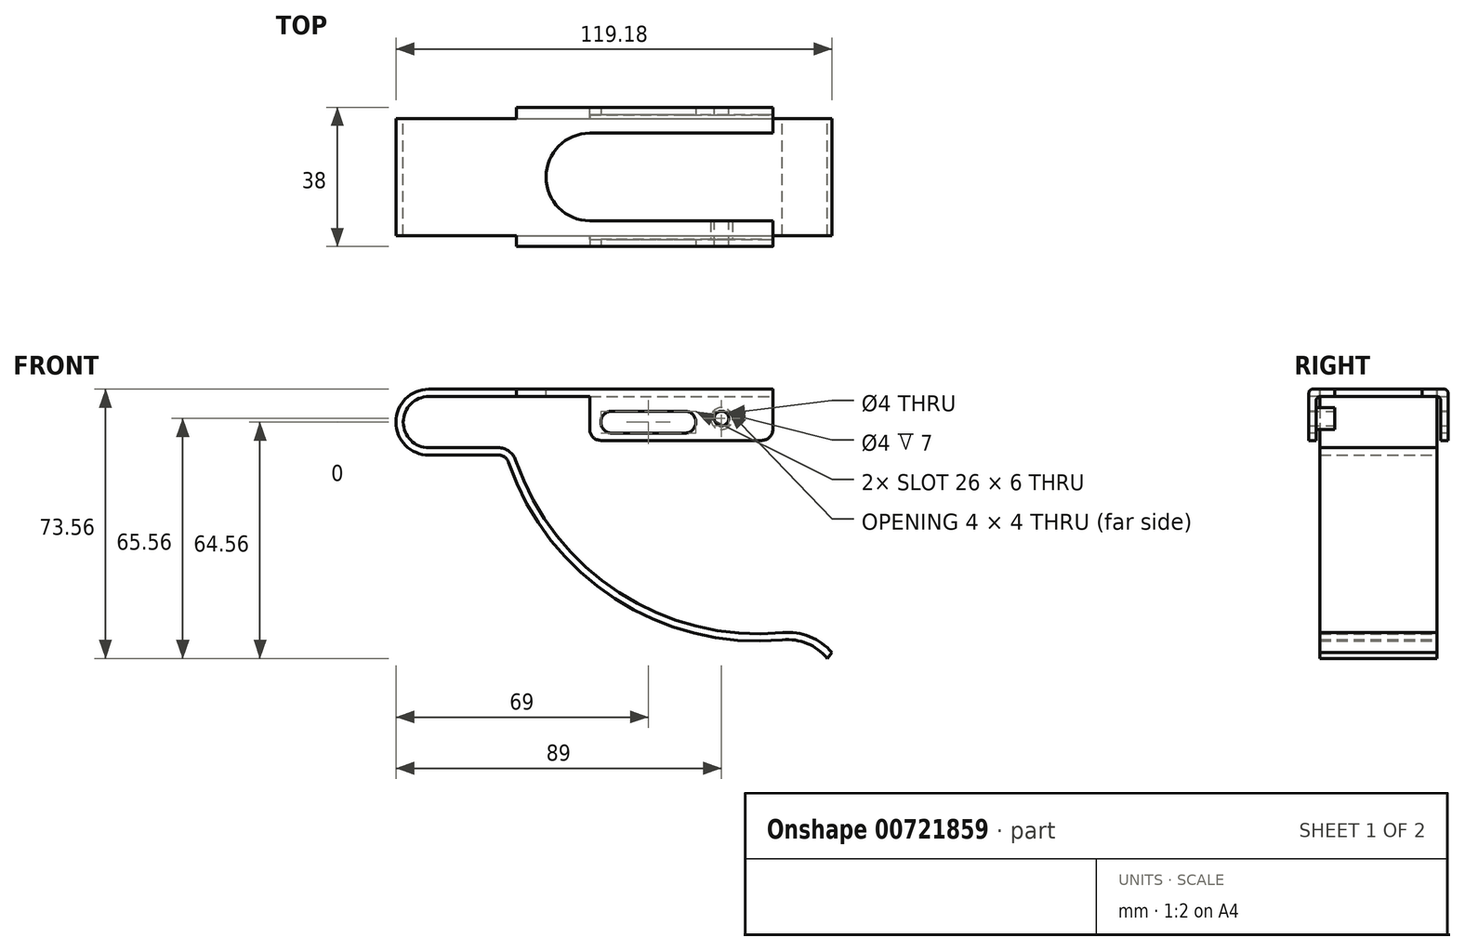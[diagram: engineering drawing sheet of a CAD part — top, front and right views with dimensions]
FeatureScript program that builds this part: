
annotation { "Feature Type Name" : "Feature", "Feature Type Description" : "" }
export const myFeature = defineFeature(function(context is Context, id is Id, definition is map)
    precondition{}
    {
        {
            var Q0;
            Q0=qCreatedBy(makeId("Front.planeOp"),FACE);
            var sketch = newSketch(context, id + "F0", { "sketchPlane" : qUnion([Q0])});
            skArc(sketch, "E0", {"start": v(0, 9) * mm, "mid": v(-9, 0) * mm, "end": v(0, -9) * mm});
            skLineSegment(sketch, "E1", {"start": v(0, 9) * mm, "end": v(94, 9) * mm});
            skLineSegment(sketch, "E2", {"start": v(0, -9) * mm, "end": v(19, -9) * mm});
            skArc(sketch, "E3", {"start": v(21.84, -11.03) * mm, "mid": v(50.83, -48.25) * mm, "end": v(96.64, -59.53) * mm});
            skArc(sketch, "E4", {"start": v(108.88, -64.56) * mm, "mid": v(103.39, -60.5) * mm, "end": v(96.64, -59.53) * mm});
            skPoint(sketch, "E5.visualSharp", {"position": v(21.18, -9) * mm});
            skArc(sketch, "E5.filletArc", {"start": v(21.84, -11.03) * mm, "mid": v(20.75, -9.56) * mm, "end": v(19, -9) * mm});
            skLineSegment(sketch, "E6.0", {"start": v(0, 7) * mm, "end": v(94, 7) * mm});
            skArc(sketch, "E6.1", {"start": v(0, 7) * mm, "mid": v(-7, 0) * mm, "end": v(0, -7) * mm});
            skArc(sketch, "E6.2", {"start": v(110.18, -63) * mm, "mid": v(104.1, -58.63) * mm, "end": v(96.7, -57.51) * mm});
            skArc(sketch, "E6.3", {"start": v(23.73, -10.39) * mm, "mid": v(52.02, -46.64) * mm, "end": v(96.7, -57.51) * mm});
            skArc(sketch, "E6.4", {"start": v(23.73, -10.39) * mm, "mid": v(21.91, -7.93) * mm, "end": v(19, -7) * mm});
            skLineSegment(sketch, "E6.5", {"start": v(0, -7) * mm, "end": v(19, -7) * mm});
            skLineSegment(sketch, "E7", {"start": v(94, 9) * mm, "end": v(94, 7) * mm});
            skLineSegment(sketch, "E8", {"start": v(110.18, -63) * mm, "end": v(108.88, -64.56) * mm});
            skSolve(sketch);
        }
        {
            var Q0;
            Q0 = qSketchRegion(id + "F0", true);
            extrude(context, id + "F1", {"entities" : qUnion([Q0]), "depth" : 16 * mm, "offsetDistance" : 25 * mm});
        }
        {
            var Q0;
            Q0=makeQuery(id+"F1.opExtrude","SWEPT_FACE",FACE,{"disambiguationData":[OSD([sQuery(id+"F0.wireOp",EDGE,"E1")])]});
            var sketch = newSketch(context, id + "F2", { "sketchPlane" : qUnion([Q0])});
            skLineSegment(sketch, "E9.bottom", {"start": v(94, -16) * mm, "end": v(24, -16) * mm});
            skLineSegment(sketch, "E9.top", {"start": v(94, -19) * mm, "end": v(24, -19) * mm});
            skLineSegment(sketch, "E9.left", {"start": v(94, -16) * mm, "end": v(94, -19) * mm});
            skLineSegment(sketch, "E9.right", {"start": v(24, -16) * mm, "end": v(24, -19) * mm});
            skSolve(sketch);
        }
        {
            var Q0;
            Q0 = qSketchRegion(id + "F2", true);
            extrude(context, id + "F3", {"entities" : qUnion([Q0]), "operationType" : NewBodyOperationType.ADD, "oppositeDirection" : true, "depth" : 2 * mm, "offsetDistance" : 25 * mm});
        }
        {
            var Q0;
            Q0=makeQuery(id+"F3.opExtrude","SWEPT_FACE",FACE,{"disambiguationData":[OSD([sQuery(id+"F2.wireOp",EDGE,"E9.top")])]});
            var sketch = newSketch(context, id + "F4", { "sketchPlane" : qUnion([Q0])});
            skLineSegment(sketch, "E10.bottom", {"start": v(94, 9) * mm, "end": v(44, 9) * mm});
            skLineSegment(sketch, "E10.top", {"start": v(94, -5) * mm, "end": v(44, -5) * mm});
            skLineSegment(sketch, "E10.left", {"start": v(94, 9) * mm, "end": v(94, -5) * mm});
            skLineSegment(sketch, "E10.right", {"start": v(44, 9) * mm, "end": v(44, -5) * mm});
            skSolve(sketch);
        }
        {
            var Q0;
            Q0 = qSketchRegion(id + "F4", true);
            extrude(context, id + "F5", {"entities" : qUnion([Q0]), "operationType" : NewBodyOperationType.ADD, "oppositeDirection" : true, "depth" : 2 * mm, "offsetDistance" : 25 * mm});
        }
        {
            var Q0;
            Q0=makeQuery(id+"F3.opExtrude","CAP_EDGE",EDGE,{"disambiguationData":[OSD([sQuery(id+"F2.wireOp",EDGE,"E9.top")])],"isStart":true});
            var Q1;
            Q1=makeQuery(id+"F5.boolean.opBoolean","INTERSECT",EDGE,{"derivedFrom":[makeQuery(id+"F3.boolean.opBoolean","MERGE",FACE,{"derivedFrom":[makeQuery(id+"F1.opExtrude","SWEPT_FACE",FACE,{"disambiguationData":[OSD([sQuery(id+"F0.wireOp",EDGE,"E6.0")])]}),makeQuery(id+"F3.opExtrude","CAP_FACE",FACE,{"disambiguationData":[OSD([sQuery(id+"F2.wireOp",EDGE,"E9.bottom"),sQuery(id+"F2.wireOp",EDGE,"E9.top"),sQuery(id+"F2.wireOp",EDGE,"E9.left"),sQuery(id+"F2.wireOp",EDGE,"E9.right")])],"isStart":false})]}),makeQuery(id+"F5.opExtrude","CAP_FACE",FACE,{"disambiguationData":[OSD([sQuery(id+"F4.wireOp",EDGE,"E10.bottom"),sQuery(id+"F4.wireOp",EDGE,"E10.top"),sQuery(id+"F4.wireOp",EDGE,"E10.left"),sQuery(id+"F4.wireOp",EDGE,"E10.right")])],"isStart":false})]});
            fillet(context, id + "F6", {"entities" : qUnion([Q0, Q1]), "radius" : 1 * mm, "allowEdgeOverflow" : false});
        }
        {
            var Q0;
            Q0=makeQuery(id+"F1.opExtrude","SWEPT_BODY",BODY,{"disambiguationData":[OSD([sQuery(id+"F0.wireOp",EDGE,"E0"),sQuery(id+"F0.wireOp",EDGE,"E1"),sQuery(id+"F0.wireOp",EDGE,"E2"),sQuery(id+"F0.wireOp",EDGE,"E3"),sQuery(id+"F0.wireOp",EDGE,"E4"),sQuery(id+"F0.wireOp",EDGE,"E5.filletArc"),sQuery(id+"F0.wireOp",EDGE,"E6.0"),sQuery(id+"F0.wireOp",EDGE,"E6.1"),sQuery(id+"F0.wireOp",EDGE,"E6.2"),sQuery(id+"F0.wireOp",EDGE,"E6.3"),sQuery(id+"F0.wireOp",EDGE,"E6.4"),sQuery(id+"F0.wireOp",EDGE,"E6.5"),sQuery(id+"F0.wireOp",EDGE,"E7"),sQuery(id+"F0.wireOp",EDGE,"E8")])]});
            var Q1;
            Q1=qCreatedBy(makeId("Front.planeOp"),FACE);
            mirror(context, id + "F7", {"operationType" : NewBodyOperationType.ADD, "entities" : qUnion([Q0]), "mirrorPlane" : qUnion([Q1])});
        }
        {
            var Q0;
            {var subQ0=makeQuery(id+"F3.boolean.opBoolean","MERGE",FACE,{"derivedFrom":[makeQuery(id+"F1.opExtrude","SWEPT_FACE",FACE,{"disambiguationData":[OSD([sQuery(id+"F0.wireOp",EDGE,"E1")])]}),makeQuery(id+"F3.opExtrude","CAP_FACE",FACE,{"disambiguationData":[OSD([sQuery(id+"F2.wireOp",EDGE,"E9.bottom"),sQuery(id+"F2.wireOp",EDGE,"E9.top"),sQuery(id+"F2.wireOp",EDGE,"E9.left"),sQuery(id+"F2.wireOp",EDGE,"E9.right")])],"isStart":true})]});Q0=makeQuery(id+"F7.boolean.opBoolean","MERGE",FACE,{"derivedFrom":[subQ0,makeQuery(id+"F7.opPattern","COPY",FACE,{"derivedFrom":subQ0,"instanceName":"1"})]});}
            var sketch = newSketch(context, id + "F8", { "sketchPlane" : qUnion([Q0])});
            skArc(sketch, "E11", {"start": v(44, 11.96) * mm, "mid": v(32.04, 0) * mm, "end": v(44, -11.96) * mm});
            skLineSegment(sketch, "E12", {"start": v(44, 11.96) * mm, "end": v(94, 11.96) * mm});
            skLineSegment(sketch, "E13", {"start": v(44, -11.96) * mm, "end": v(94, -11.96) * mm});
            skLineSegment(sketch, "E14", {"start": v(94, 11.96) * mm, "end": v(94, -11.96) * mm});
            skSolve(sketch);
        }
        {
            var Q0;
            Q0 = qSketchRegion(id + "F8", true);
            extrude(context, id + "F9", {"entities" : qUnion([Q0]), "operationType" : NewBodyOperationType.REMOVE, "oppositeDirection" : true, "depth" : 2 * mm, "offsetDistance" : 25 * mm});
        }
        {
            var Q0;
            Q0=makeQuery(id+"F5.boolean.opBoolean","MERGE",FACE,{"derivedFrom":[makeQuery(id+"F3.opExtrude","SWEPT_FACE",FACE,{"disambiguationData":[OSD([sQuery(id+"F2.wireOp",EDGE,"E9.top")])]}),makeQuery(id+"F5.opExtrude","CAP_FACE",FACE,{"disambiguationData":[OSD([sQuery(id+"F4.wireOp",EDGE,"E10.bottom"),sQuery(id+"F4.wireOp",EDGE,"E10.top"),sQuery(id+"F4.wireOp",EDGE,"E10.left"),sQuery(id+"F4.wireOp",EDGE,"E10.right")])],"isStart":true})]});
            var sketch = newSketch(context, id + "F10", { "sketchPlane" : qUnion([Q0])});
            skLineSegment(sketch, "E15", {"start": v(50, 0) * mm, "end": v(70, 0) * mm});
            skArc(sketch, "E16.0.startCap", {"start": v(50, -3) * mm, "mid": v(47, 0) * mm, "end": v(50, 3) * mm});
            skArc(sketch, "E16.0.endCap", {"start": v(70, 3) * mm, "mid": v(73, 0) * mm, "end": v(70, -3) * mm});
            skLineSegment(sketch, "E16.0.left", {"start": v(50, 3) * mm, "end": v(70, 3) * mm});
            skLineSegment(sketch, "E16.0.right", {"start": v(50, -3) * mm, "end": v(70, -3) * mm});
            skSolve(sketch);
        }
        {
            var Q0;
            Q0 = qSketchRegion(id + "F10", true);
            extrude(context, id + "F11", {"entities" : qUnion([Q0]), "operationType" : NewBodyOperationType.REMOVE, "endBound" : BoundingType.THROUGH_ALL, "oppositeDirection" : true, "depth" : 25 * mm, "offsetDistance" : 25 * mm});
        }
        {
            var Q0;
            Q0=makeQuery(id+"F5.boolean.opBoolean","MERGE",FACE,{"derivedFrom":[makeQuery(id+"F3.opExtrude","SWEPT_FACE",FACE,{"disambiguationData":[OSD([sQuery(id+"F2.wireOp",EDGE,"E9.top")])]}),makeQuery(id+"F5.opExtrude","CAP_FACE",FACE,{"disambiguationData":[OSD([sQuery(id+"F4.wireOp",EDGE,"E10.bottom"),sQuery(id+"F4.wireOp",EDGE,"E10.top"),sQuery(id+"F4.wireOp",EDGE,"E10.left"),sQuery(id+"F4.wireOp",EDGE,"E10.right")])],"isStart":true})]});
            var sketch = newSketch(context, id + "F12", { "sketchPlane" : qUnion([Q0])});
            skPoint(sketch, "E17", {"position": v(80, 1) * mm});
            skSolve(sketch);
        }
        {
            var Q0;
            Q0=sQuery(id+"F12.wireOp",VERTEX,"E17");
            var Q1;
            Q1=makeQuery(id+"F1.opExtrude","SWEPT_BODY",BODY,{"disambiguationData":[OSD([sQuery(id+"F0.wireOp",EDGE,"E0"),sQuery(id+"F0.wireOp",EDGE,"E1"),sQuery(id+"F0.wireOp",EDGE,"E2"),sQuery(id+"F0.wireOp",EDGE,"E3"),sQuery(id+"F0.wireOp",EDGE,"E4"),sQuery(id+"F0.wireOp",EDGE,"E5.filletArc"),sQuery(id+"F0.wireOp",EDGE,"E6.0"),sQuery(id+"F0.wireOp",EDGE,"E6.1"),sQuery(id+"F0.wireOp",EDGE,"E6.2"),sQuery(id+"F0.wireOp",EDGE,"E6.3"),sQuery(id+"F0.wireOp",EDGE,"E6.4"),sQuery(id+"F0.wireOp",EDGE,"E6.5"),sQuery(id+"F0.wireOp",EDGE,"E7"),sQuery(id+"F0.wireOp",EDGE,"E8")])]});
            hole(context, id + "F13", {"style" : HoleStyle.SIMPLE, "endStyle" : HoleEndStyle.THROUGH, "holeDiameter" : 4 * mm, "majorDiameter" : 5 * mm, "isTappedThrough" : true, "tappedDepth" : 12 * mm, "tapClearance" : 3, "locations" : qUnion([Q0]), "scope" : qUnion([Q1]), "startStyle" : HoleStartStyle.PART});
        }
        {
            var Q0;
            Q0=makeQuery(id+"F5.opExtrude","CAP_FACE",FACE,{"disambiguationData":[OSD([sQuery(id+"F4.wireOp",EDGE,"E10.bottom"),sQuery(id+"F4.wireOp",EDGE,"E10.top"),sQuery(id+"F4.wireOp",EDGE,"E10.left"),sQuery(id+"F4.wireOp",EDGE,"E10.right")])],"isStart":false});
            var sketch = newSketch(context, id + "F14", { "sketchPlane" : qUnion([Q0])});
            skCircle(sketch, "E18.0", {"center": v(-80, 1) * mm, "radius": 3 * mm});
            skSolve(sketch);
        }
        {
            var Q0;
            Q0=makeQuery(id+"F14.imprint","IMPRINT",FACE,{"disambiguationData":[TD([[makeQuery(id+"F14.imprint","IMPRINT",EDGE,{"derivedFrom":sQuery(id+"F14.wireOp",EDGE,"E18.0")}),1.0]])]});
            extrude(context, id + "F15", {"entities" : qUnion([Q0]), "operationType" : NewBodyOperationType.ADD, "depth" : 5 * mm, "offsetDistance" : 25 * mm});
        }
        {
            var Q0;
            Q0=makeQuery(id+"F7.opPattern","COPY",EDGE,{"derivedFrom":makeQuery(id+"F5.opExtrude","SWEPT_EDGE",EDGE,{"disambiguationData":[OSD([sQuery(id+"F4.wireOp",EDGE,"E10.top"),sQuery(id+"F4.wireOp",EDGE,"E10.left")])]}),"instanceName":"1"});
            var Q1;
            Q1=makeQuery(id+"F5.opExtrude","SWEPT_EDGE",EDGE,{"disambiguationData":[OSD([sQuery(id+"F4.wireOp",EDGE,"E10.top"),sQuery(id+"F4.wireOp",EDGE,"E10.left")])]});
            var Q2;
            Q2=makeQuery(id+"F5.opExtrude","SWEPT_EDGE",EDGE,{"disambiguationData":[OSD([sQuery(id+"F4.wireOp",EDGE,"E10.top"),sQuery(id+"F4.wireOp",EDGE,"E10.right")])]});
            var Q3;
            Q3=makeQuery(id+"F7.opPattern","COPY",EDGE,{"derivedFrom":makeQuery(id+"F5.opExtrude","SWEPT_EDGE",EDGE,{"disambiguationData":[OSD([sQuery(id+"F4.wireOp",EDGE,"E10.top"),sQuery(id+"F4.wireOp",EDGE,"E10.right")])]}),"instanceName":"1"});
            fillet(context, id + "F16", {"entities" : qUnion([Q0, Q1, Q2, Q3]), "radius" : 3 * mm, "tangentPropagation" : true, "allowEdgeOverflow" : false});
        }
    });
